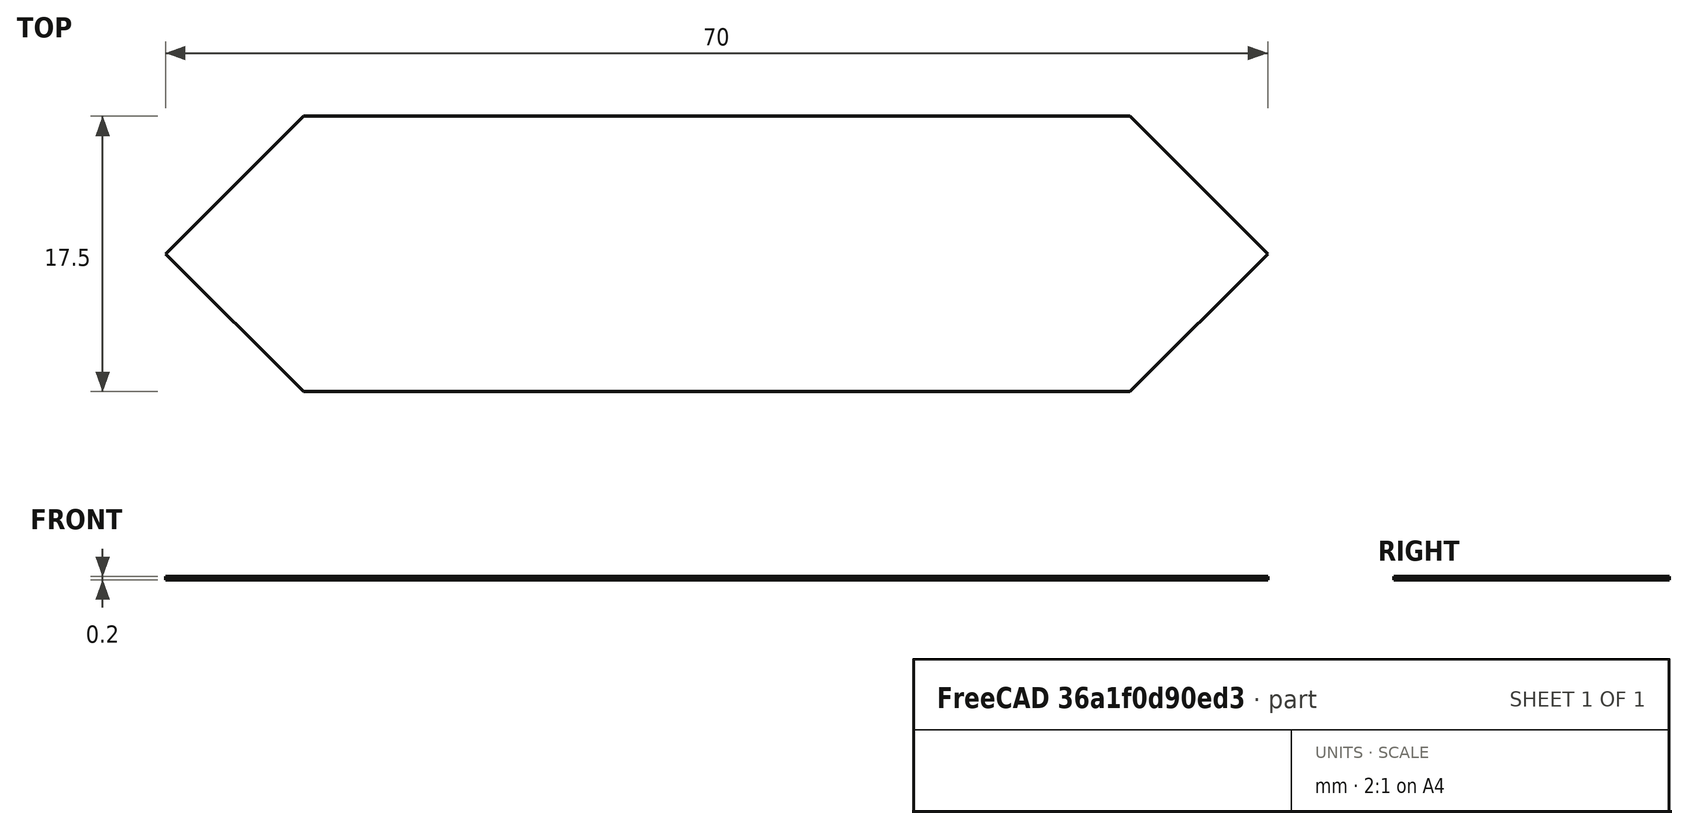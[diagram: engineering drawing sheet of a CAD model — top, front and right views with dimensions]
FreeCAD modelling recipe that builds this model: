
FCSTD DOCUMENT  (FreeCAD 0.20R29603 (Git))
Label: FacePlate_70x17
License: All rights reserved
LicenseURL: http://en.wikipedia.org/wiki/All_rights_reserved
objects: Sketcher::SketchObject×1, PartDesign::Pad×1, PartDesign::Body×1
note: 4 computed .brp shape members not serialized (recipe doc carries the construction recipe); baked Part::Feature solids carry a one-line shape summary decoded from their .brp

FEATURE [Sketcher::SketchObject] Sketch
  FullyConstrained = true
  MapMode = 5
  Support = -> [XY_Plane]
  sketch-geometry (6):
    g0: LineSegment StartX=-26.25 StartY=8.75 StartZ=0 EndX=26.25 EndY=8.75 EndZ=0
    g1: LineSegment StartX=-26.25 StartY=-8.75 StartZ=0 EndX=26.25 EndY=-8.75 EndZ=0
    g2: LineSegment StartX=26.25 StartY=8.75 StartZ=0 EndX=35 EndY=0 EndZ=0
    g3: LineSegment StartX=26.25 StartY=-8.75 StartZ=0 EndX=35 EndY=0 EndZ=0
    g4: LineSegment StartX=-26.25 StartY=-8.75 StartZ=0 EndX=-35 EndY=0 EndZ=0
    g5: LineSegment StartX=-26.25 StartY=8.75 StartZ=0 EndX=-35 EndY=0 EndZ=0
  constraints (16):
    c: Horizontal(g0)
    c: Horizontal(g1)
    c: Coincident(g2,g0)
    c: PointOnObject(g2,g-1)
    c: Coincident(g3,g1)
    c: Coincident(g3,g2)
    c: Coincident(g4,g1)
    c: Coincident(g5,g0)
    c: Coincident(g5,g4)
    c: Angle(g4,g5) = 1.5708
    c: DistanceY(g1,g0) = 17.5
    c: Angle(g2,g3) = 1.5708
    c: Symmetric(g0,g1,g-1)
    c: Equal(g0,g1)
    c: Symmetric(g4,g2,g-2)
    c: DistanceX(g4,g2) = 70
FEATURE [PartDesign::Pad] Pad  label="Face"
  Direction = (0,0,1)
  Length = 0.2
  Length2 = 100
  Profile = -> Sketch
  Type = 0
FEATURE [PartDesign::Body] Body
  Group = -> [Sketch,Pad]
  Origin = -> Origin
  Tip = -> Pad
